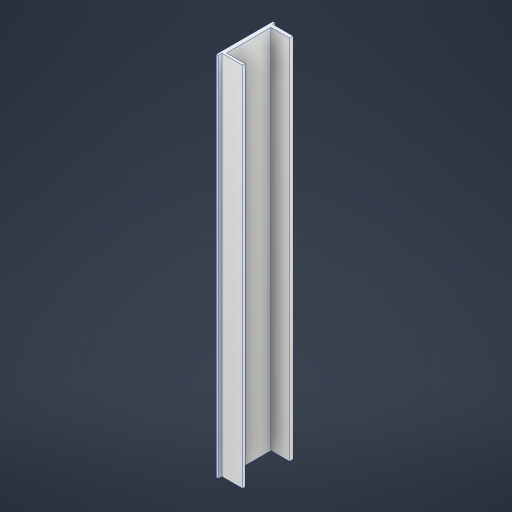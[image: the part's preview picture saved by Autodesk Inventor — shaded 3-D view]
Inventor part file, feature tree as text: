
AUTODESK INVENTOR PART (.ipt)
format: ipt  version: 2024 (Build 280153000, 153)  size: 254,976 bytes
history: native  units: mm
features: extrude x1, sketch x1
ambient origin geometry x8: Origin, YZ Plane, XZ Plane, XY Plane, X Axis, Y Axis, Z Axis, Center Point
bodies: Solid1 (feature_tree)
feature tree (2):
  extrude  "Extrusion1"  Depth=711.0mm TaperAngle=0.0deg
  sketch  "Sketch1"  dims[d0=110.0mm d1=711.0mm d2=0.0mm]
